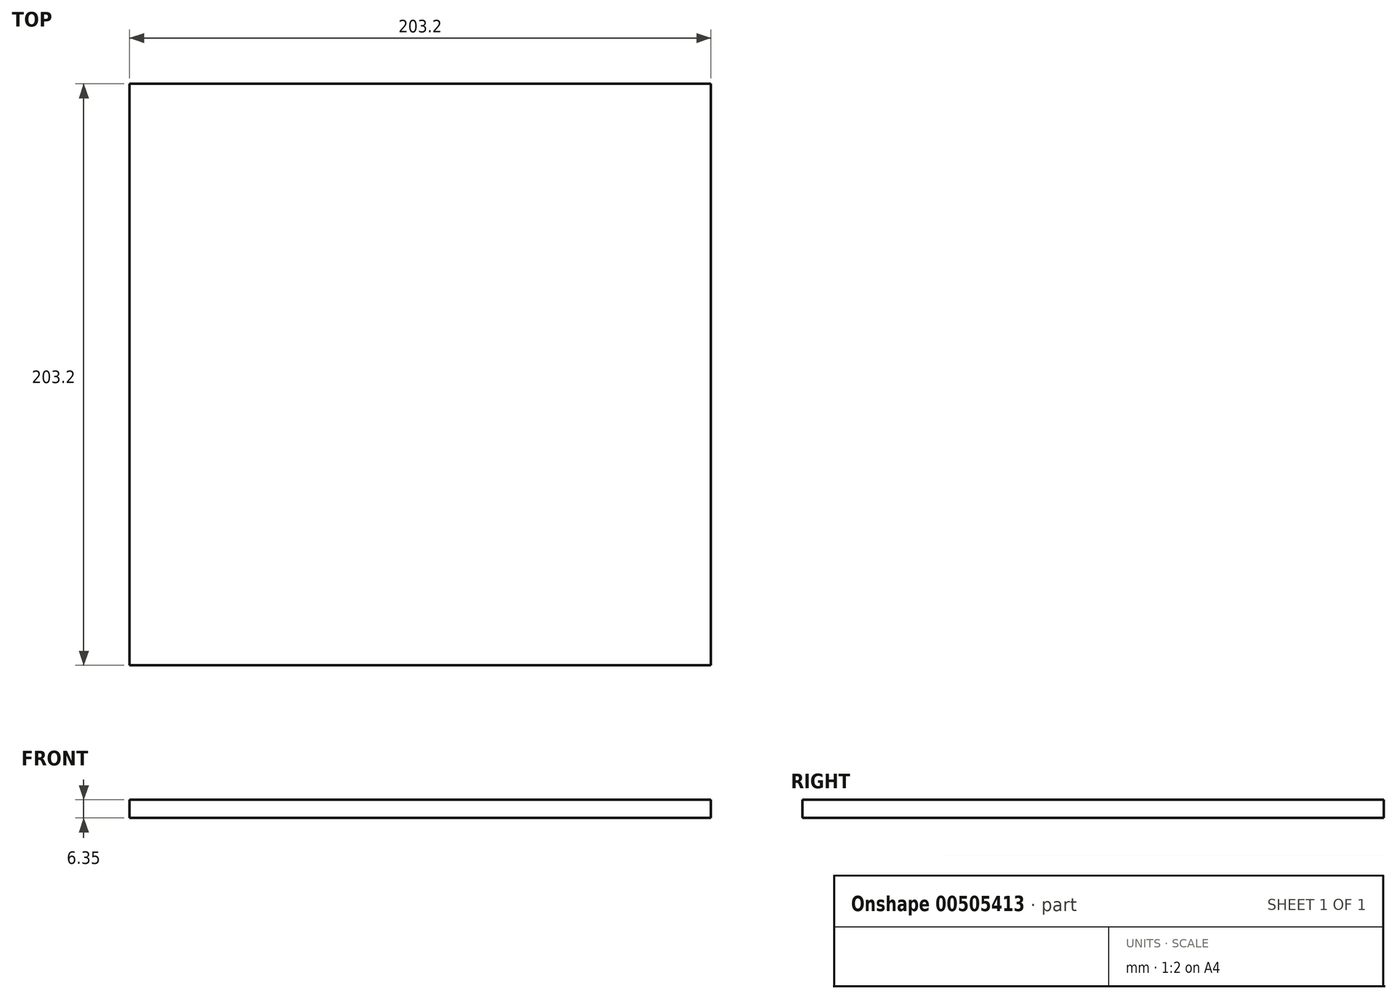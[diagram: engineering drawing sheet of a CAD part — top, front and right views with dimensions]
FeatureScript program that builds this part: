
annotation { "Feature Type Name" : "Feature", "Feature Type Description" : "" }
export const myFeature = defineFeature(function(context is Context, id is Id, definition is map)
    precondition{}
    {
        {
            var Q0;
            Q0=qCreatedBy(makeId("Top.planeOp"),FACE);
            var sketch = newSketch(context, id + "F0", { "sketchPlane" : qUnion([Q0])});
            skLineSegment(sketch, "E0.bottom", {"start": v(-101.6, 101.6) * mm, "end": v(101.6, 101.6) * mm});
            skLineSegment(sketch, "E0.top", {"start": v(-101.6, -101.6) * mm, "end": v(101.6, -101.6) * mm});
            skLineSegment(sketch, "E0.left", {"start": v(-101.6, 101.6) * mm, "end": v(-101.6, -101.6) * mm});
            skLineSegment(sketch, "E0.right", {"start": v(101.6, 101.6) * mm, "end": v(101.6, -101.6) * mm});
            skPoint(sketch, "E0.middle", {"position": v(0, 0) * mm});
            skSolve(sketch);
        }
        {
            var Q0;
            Q0=makeQuery(id+"F0.imprint","IMPRINT",FACE,{"disambiguationData":[TD([[makeQuery(id+"F0.imprint","IMPRINT",EDGE,{"derivedFrom":sQuery(id+"F0.wireOp",EDGE,"E0.bottom")}),-1.0]])]});
            extrude(context, id + "F1", {"entities" : qUnion([Q0]), "depth" : 6.35 * mm, "offsetDistance" : 25.4 * mm});
        }
    });
